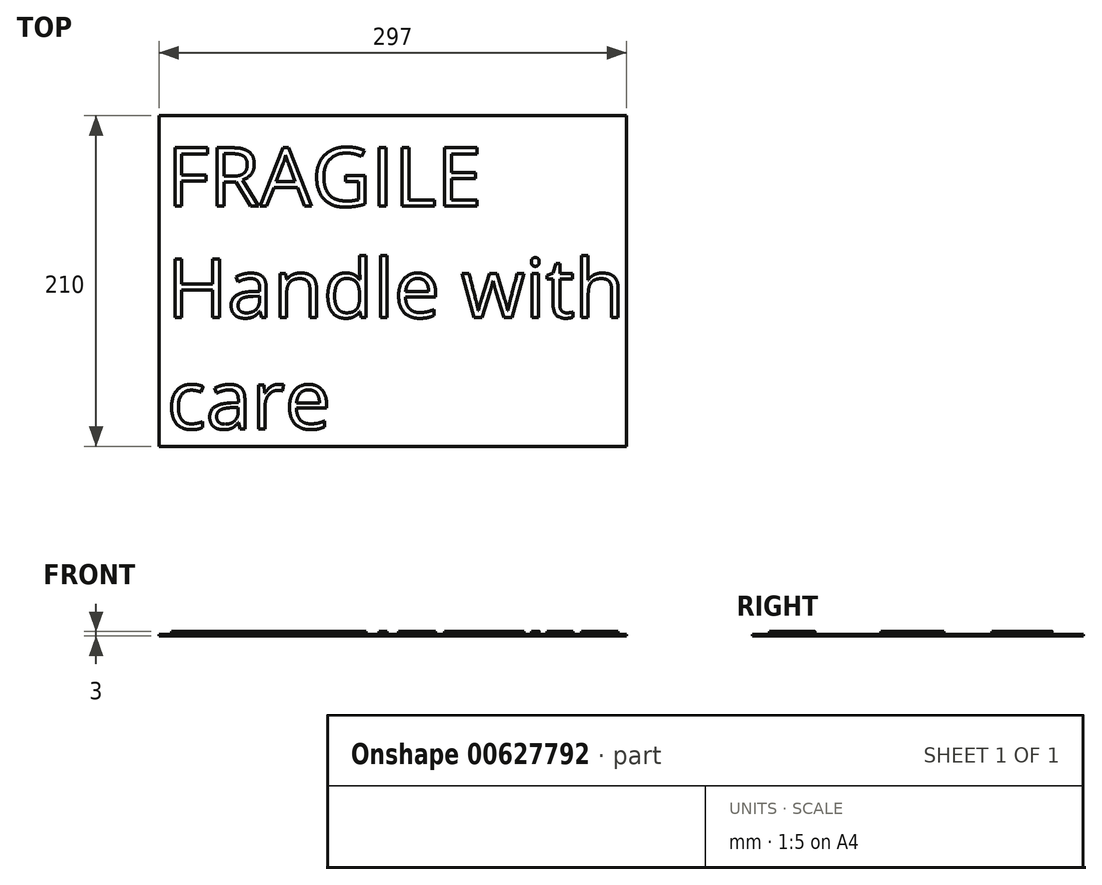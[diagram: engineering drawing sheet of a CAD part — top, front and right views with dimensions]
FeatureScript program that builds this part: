
annotation { "Feature Type Name" : "Feature", "Feature Type Description" : "" }
export const myFeature = defineFeature(function(context is Context, id is Id, definition is map)
    precondition{}
    {
        {
            var Q0;
            Q0=qCreatedBy(makeId("Top.planeOp"),FACE);
            var sketch = newSketch(context, id + "F0", { "sketchPlane" : qUnion([Q0])});
            skLineSegment(sketch, "E0.bottom", {"start": v(-226.49, 160.02) * mm, "end": v(70.51, 160.02) * mm});
            skLineSegment(sketch, "E0.top", {"start": v(-226.49, -49.98) * mm, "end": v(70.51, -49.98) * mm});
            skLineSegment(sketch, "E0.left", {"start": v(-226.49, 160.02) * mm, "end": v(-226.49, -49.98) * mm});
            skLineSegment(sketch, "E0.right", {"start": v(70.51, 160.02) * mm, "end": v(70.51, -49.98) * mm});
            skSolve(sketch);
        }
        {
            var Q0;
            Q0 = qSketchRegion(id + "F0", true);
            extrude(context, id + "F1", {"entities" : qUnion([Q0]), "depth" : 1 * mm, "offsetDistance" : 25 * mm});
        }
        {
            var Q0;
            Q0=makeQuery(id+"F1.opExtrude","CAP_FACE",FACE,{"disambiguationData":[OSD([sQuery(id+"F0.wireOp",EDGE,"E0.bottom"),sQuery(id+"F0.wireOp",EDGE,"E0.top"),sQuery(id+"F0.wireOp",EDGE,"E0.left"),sQuery(id+"F0.wireOp",EDGE,"E0.right")])],"isStart":false});
            var sketch = newSketch(context, id + "F2", { "sketchPlane" : qUnion([Q0])});
            skText(sketch, "E1", { "text": "FRAGILE\nHandle with\ncare", "fontName": "OpenSans-Regular.ttf"});
            const initialGuessF2  = {"E1": [-0.22149, 0.10257, 1, 0, 0.03744]};
            skSetInitialGuess(sketch, initialGuessF2);
            skSolve(sketch);
        }
        {
            var Q0;
            Q0 = qSketchRegion(id + "F2", true);
            extrude(context, id + "F3", {"entities" : qUnion([Q0]), "operationType" : NewBodyOperationType.ADD, "depth" : 2 * mm, "offsetDistance" : 25 * mm});
        }
    });
